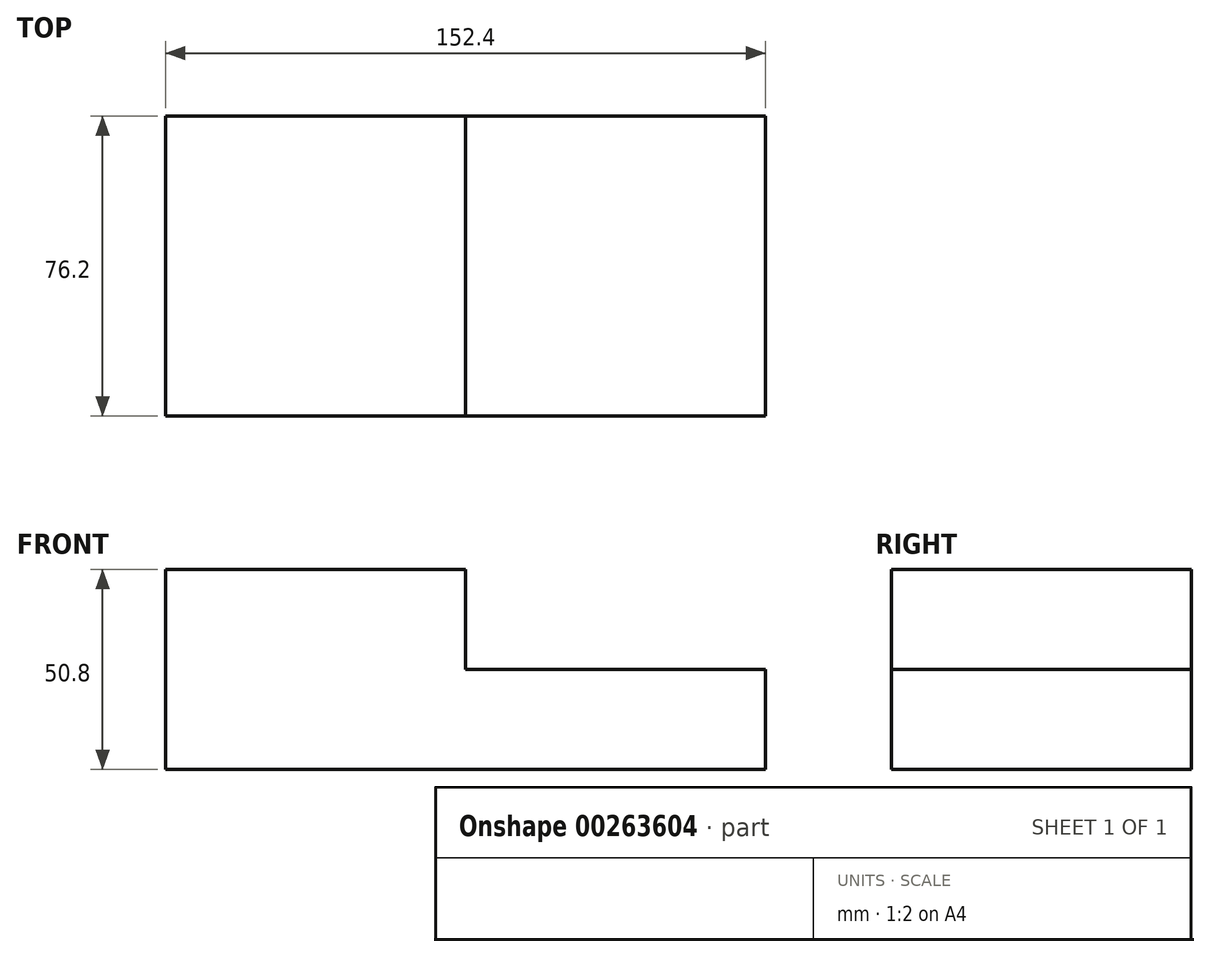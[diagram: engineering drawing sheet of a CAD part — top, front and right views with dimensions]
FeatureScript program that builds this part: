
annotation { "Feature Type Name" : "Feature", "Feature Type Description" : "" }
export const myFeature = defineFeature(function(context is Context, id is Id, definition is map)
    precondition{}
    {
        {
            var Q0;
            Q0=qCreatedBy(makeId("Front.planeOp"),FACE);
            var sketch = newSketch(context, id + "F0", { "sketchPlane" : qUnion([Q0])});
            skLineSegment(sketch, "E0.right", {"start": v(1.95, 25.4) * mm, "end": v(1.95, 50.8) * mm});
            skLineSegment(sketch, "E1", {"start": v(-74.25, 50.8) * mm, "end": v(-74.25, 0) * mm});
            skLineSegment(sketch, "E2", {"start": v(-74.25, 0) * mm, "end": v(78.15, 0) * mm});
            skLineSegment(sketch, "E3", {"start": v(78.15, 25.4) * mm, "end": v(78.15, 0) * mm});
            skLineSegment(sketch, "E4", {"start": v(1.95, 25.4) * mm, "end": v(78.15, 25.4) * mm});
            skLineSegment(sketch, "E5", {"start": v(-74.25, 50.8) * mm, "end": v(1.95, 50.8) * mm});
            skSolve(sketch);
        }
        {
            var Q0;
            Q0 = qSketchRegion(id + "F0", true);
            extrude(context, id + "F1", {"entities" : qUnion([Q0]), "depth" : 76.2 * mm});
        }
    });
